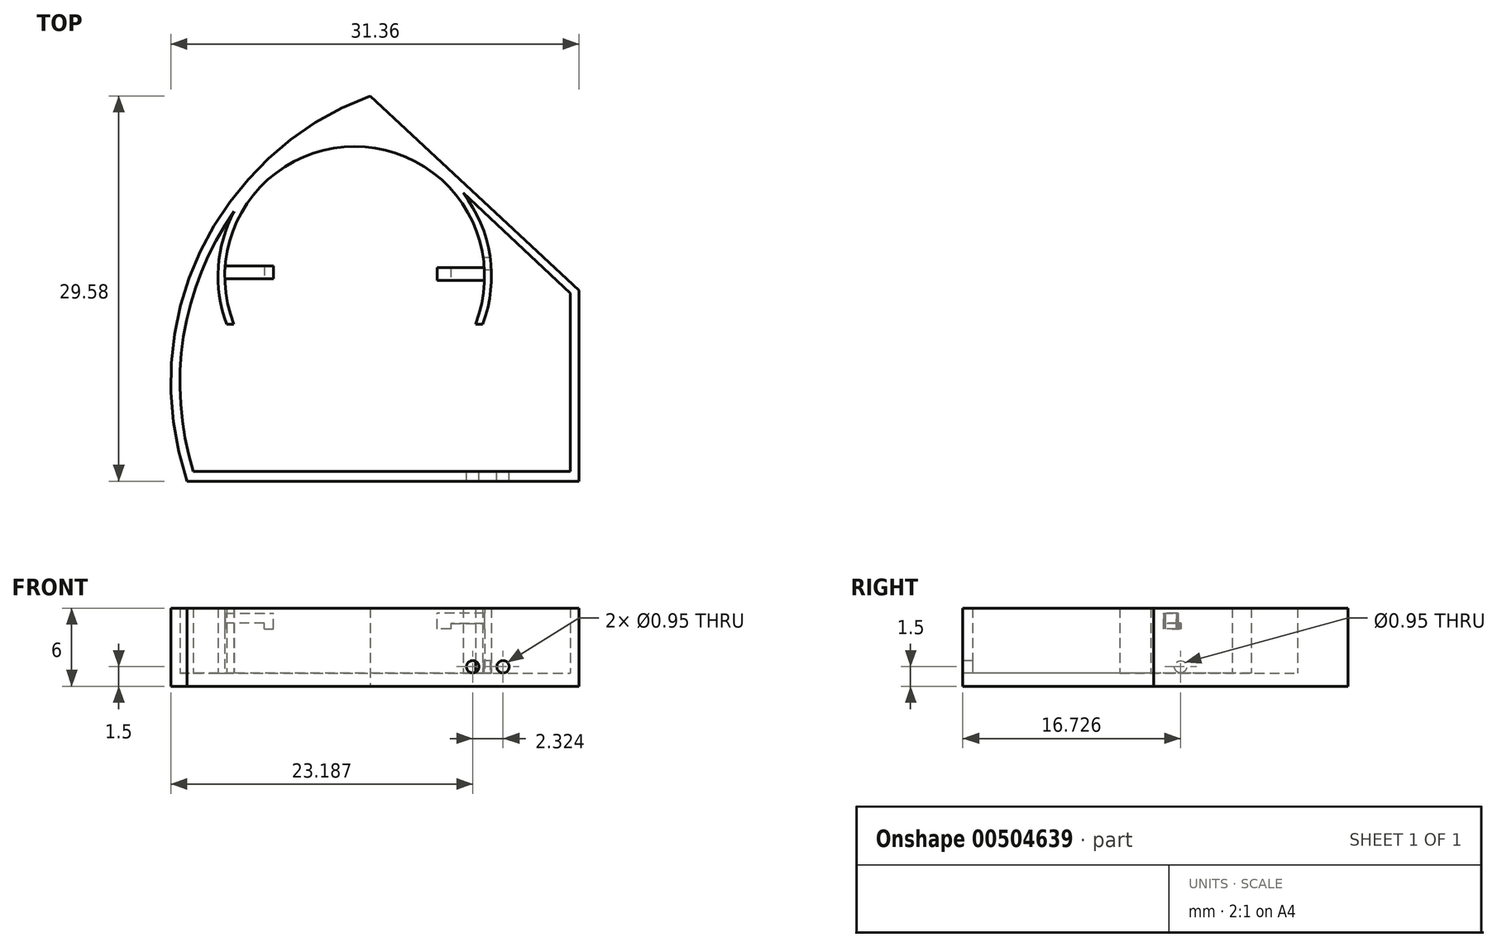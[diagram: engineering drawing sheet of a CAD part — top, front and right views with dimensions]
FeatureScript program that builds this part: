
annotation { "Feature Type Name" : "Feature", "Feature Type Description" : "" }
export const myFeature = defineFeature(function(context is Context, id is Id, definition is map)
    precondition{}
    {
        {
            var Q0;
            Q0=qCreatedBy(makeId("Top.planeOp"),FACE);
            var sketch = newSketch(context, id + "F0", { "sketchPlane" : qUnion([Q0])});
            skCircle(sketch, "E0", {"center": v(-9.38, 8.18) * mm, "radius": 9.97 * mm});
            skArc(sketch, "E1", {"start": v(-3.54, 16.9) * mm, "mid": v(-16.56, 0.52) * mm, "end": v(-1.05, 14.58) * mm});
            skArc(sketch, "E2", {"start": v(-18.63, 13.15) * mm, "mid": v(-22.58, 3.14) * mm, "end": v(-21.5, -7.56) * mm});
            skLineSegment(sketch, "E3", {"start": v(-21.76, -6.8) * mm, "end": v(7.86, -6.8) * mm});
            skLineSegment(sketch, "E4", {"start": v(-1.05, 14.58) * mm, "end": v(7.86, 6.22) * mm});
            skLineSegment(sketch, "E5", {"start": v(-1.05, 14.58) * mm, "end": v(-8.2, 21.27) * mm});
            skArc(sketch, "E6", {"start": v(-8.2, 22.02) * mm, "mid": v(-21.23, 10.08) * mm, "end": v(-22.25, -7.56) * mm});
            skLineSegment(sketch, "E7", {"start": v(-22.25, -7.56) * mm, "end": v(7.86, -7.56) * mm});
            skLineSegment(sketch, "E8", {"start": v(-8.2, 22.02) * mm, "end": v(7.86, 7.1) * mm});
            skLineSegment(sketch, "E9", {"start": v(7.18, 7.73) * mm, "end": v(7.18, -7.56) * mm});
            skLineSegment(sketch, "E10", {"start": v(7.86, 6.22) * mm, "end": v(7.86, -6.8) * mm});
            skLineSegment(sketch, "E11", {"start": v(7.86, 6.22) * mm, "end": v(7.86, 7.1) * mm});
            skLineSegment(sketch, "E12", {"start": v(7.86, -6.8) * mm, "end": v(7.86, -7.56) * mm});
            skLineSegment(sketch, "E13", {"start": v(-19.22, 4.5) * mm, "end": v(-18.65, 4.5) * mm});
            skLineSegment(sketch, "E14", {"start": v(-0.1, 4.5) * mm, "end": v(0.46, 4.5) * mm});
            skArc(sketch, "E15.trimOffspring", {"start": v(-7.63, 21.49) * mm, "mid": v(-7.91, 21.38) * mm, "end": v(-8.2, 21.27) * mm});
            skPoint(sketch, "E16.trimOffspring.end.orphan", {"position": v(22.56, -6.57) * mm});
            skSolve(sketch);
        }
        {
            var Q0;
            Q0=qCreatedBy(makeId("Top.planeOp"),FACE);
            cPlane(context, id + "F1", {"entities" : qUnion([Q0]), "cplaneType" : CPlaneType.OFFSET, "offset" : 5.6 * mm, "width" : 150 * mm, "height" : 150 * mm});
        }
        {
            var Q0;
            {var subQ0=sQuery(id+"F0.wireOp",EDGE,"E10");Q0=makeQuery(id+"F0.imprint","IMPRINT",FACE,{"disambiguationData":[TD([[makeQuery(id+"F0.imprint","IMPRINT",EDGE,{"derivedFrom":subQ0}),-1.0]])]});}
            var Q1;
            {var subQ0=sQuery(id+"F0.wireOp",EDGE,"E3");var subQ1=sQuery(id+"F0.wireOp",EDGE,"E2");var subQ2=makeQuery(id+"F0.imprint","INTERSECT",VERTEX,{"derivedFrom":[subQ1,subQ0]});Q1=makeQuery(id+"F0.imprint","IMPRINT",FACE,{"disambiguationData":[TD([[makeQuery(id+"F0.imprint","IMPRINT",EDGE,{"disambiguationData":[TD([[subQ2,-1.0]])],"derivedFrom":subQ1}),1.0]])]});}
            var Q2;
            {var subQ0=sQuery(id+"F0.wireOp",EDGE,"E11");Q2=makeQuery(id+"F0.imprint","IMPRINT",FACE,{"disambiguationData":[TD([[makeQuery(id+"F0.imprint","IMPRINT",EDGE,{"derivedFrom":subQ0}),1.0]])]});}
            var Q3;
            {var subQ0=sQuery(id+"F0.wireOp",EDGE,"E5");var subQ3=sQuery(id+"F0.wireOp",EDGE,"E2");var subQ4=makeQuery(id+"F0.imprint","INTERSECT",VERTEX,{"derivedFrom":[subQ3,subQ0]});Q3=makeQuery(id+"F0.imprint","IMPRINT",FACE,{"disambiguationData":[TD([[makeQuery(id+"F0.imprint","IMPRINT",EDGE,{"disambiguationData":[TD([[subQ4,1.0]])],"derivedFrom":subQ3}),1.0]])]});}
            var Q4;
            {var subQ0=sQuery(id+"F0.wireOp",EDGE,"E12");Q4=makeQuery(id+"F0.imprint","IMPRINT",FACE,{"disambiguationData":[TD([[makeQuery(id+"F0.imprint","IMPRINT",EDGE,{"derivedFrom":subQ0}),-1.0]])]});}
            var Q5;
            {var subQ0=sQuery(id+"F0.wireOp",EDGE,"E5");var subQ8=sQuery(id+"F0.wireOp",EDGE,"E1");var subQ10=makeQuery(id+"F0.imprint","INTERSECT",VERTEX,{"derivedFrom":[subQ8,subQ0]});Q5=makeQuery(id+"F0.imprint","IMPRINT",FACE,{"disambiguationData":[TD([[makeQuery(id+"F0.imprint","IMPRINT",EDGE,{"disambiguationData":[TD([[subQ10,-1.0]])],"derivedFrom":subQ8}),-1.0]])]});}
            var Q6;
            {var subQ4=sQuery(id+"F0.wireOp",EDGE,"zcf4CaVi-9V9S-3gAH-KYeD-Rh70sNSUDDbX");Q6=makeQuery(id+"F0.imprint","IMPRINT",FACE,{"disambiguationData":[TD([[makeQuery(id+"F0.imprint","IMPRINT",EDGE,{"derivedFrom":subQ4}),-1.0]])]});}
            var Q7;
            {var subQ5=sQuery(id+"F0.wireOp",EDGE,"E13");Q7=makeQuery(id+"F0.imprint","IMPRINT",FACE,{"disambiguationData":[TD([[makeQuery(id+"F0.imprint","IMPRINT",EDGE,{"derivedFrom":subQ5}),1.0]])]});}
            var Q8;
            {var subQ3=sQuery(id+"F0.wireOp",EDGE,"E15.trimOffspring");Q8=makeQuery(id+"F0.imprint","IMPRINT",FACE,{"disambiguationData":[TD([[makeQuery(id+"F0.imprint","IMPRINT",EDGE,{"derivedFrom":subQ3}),1.0]])]});}
            extrude(context, id + "F2", {"entities" : qUnion([Q0, Q1, Q2, Q3, Q4, Q5, Q6, Q7, Q8]), "depth" : 6 * mm, "offsetDistance" : 25 * mm});
        }
        {
            var Q0;
            Q0=makeQuery(id+"F2.opExtrude","SWEPT_FACE",FACE,{"disambiguationData":[OSD([sQuery(id+"F0.wireOp",EDGE,"E3")])]});
            var sketch = newSketch(context, id + "F3", { "sketchPlane" : qUnion([Q0])});
            skCircle(sketch, "E17", {"center": v(0.31, 1.5) * mm, "radius": 0.47 * mm});
            skCircle(sketch, "E18", {"center": v(-2.01, 1.5) * mm, "radius": 0.47 * mm});
            skSolve(sketch);
        }
        {
            var Q0;
            Q0=qCreatedBy(id+"F1.planeOp",FACE);
            var sketch = newSketch(context, id + "F4", { "sketchPlane" : qUnion([Q0])});
            skLineSegment(sketch, "E19.bottom", {"start": v(-19.62, 8.98) * mm, "end": v(-15.62, 8.98) * mm});
            skLineSegment(sketch, "E19.top", {"start": v(-19.62, 7.98) * mm, "end": v(-15.62, 7.98) * mm});
            skLineSegment(sketch, "E19.left", {"start": v(-19.62, 8.98) * mm, "end": v(-19.62, 7.98) * mm});
            skLineSegment(sketch, "E19.right", {"start": v(-15.62, 8.98) * mm, "end": v(-15.62, 7.98) * mm});
            skLineSegment(sketch, "E20.bottom", {"start": v(0.96, 8.85) * mm, "end": v(-3.04, 8.85) * mm});
            skLineSegment(sketch, "E20.top", {"start": v(0.96, 7.85) * mm, "end": v(-3.04, 7.85) * mm});
            skLineSegment(sketch, "E20.left", {"start": v(0.96, 8.85) * mm, "end": v(0.96, 7.85) * mm});
            skLineSegment(sketch, "E20.right", {"start": v(-3.04, 8.85) * mm, "end": v(-3.04, 7.85) * mm});
            skSolve(sketch);
        }
        {
            var Q0;
            Q0=makeQuery(id+"F4.imprint","IMPRINT",FACE,{"disambiguationData":[TD([[makeQuery(id+"F4.imprint","IMPRINT",EDGE,{"derivedFrom":sQuery(id+"F4.wireOp",EDGE,"E20.bottom")}),1.0]])]});
            var Q1;
            Q1=makeQuery(id+"F4.imprint","IMPRINT",FACE,{"disambiguationData":[TD([[makeQuery(id+"F4.imprint","IMPRINT",EDGE,{"derivedFrom":sQuery(id+"F4.wireOp",EDGE,"E19.bottom")}),-1.0]])]});
            extrude(context, id + "F5", {"entities" : qUnion([Q0, Q1]), "operationType" : NewBodyOperationType.ADD, "oppositeDirection" : true, "depth" : 1.2 * mm, "offsetDistance" : 25 * mm});
        }
        {
            var Q0;
            Q0=makeQuery(id+"F3.imprint","IMPRINT",FACE,{"disambiguationData":[TD([[makeQuery(id+"F3.imprint","IMPRINT",EDGE,{"derivedFrom":sQuery(id+"F3.wireOp",EDGE,"E17")}),1.0]])]});
            var Q1;
            Q1=makeQuery(id+"F3.imprint","IMPRINT",FACE,{"disambiguationData":[TD([[makeQuery(id+"F3.imprint","IMPRINT",EDGE,{"derivedFrom":sQuery(id+"F3.wireOp",EDGE,"E18")}),1.0]])]});
            extrude(context, id + "F6", {"entities" : qUnion([Q0, Q1]), "operationType" : NewBodyOperationType.REMOVE, "oppositeDirection" : true, "depth" : 1 * mm, "offsetDistance" : 25 * mm});
        }
        {
            var Q0;
            Q0=makeQuery(id+"F5.opExtrude","SWEPT_FACE",FACE,{"disambiguationData":[OSD([sQuery(id+"F4.wireOp",EDGE,"E19.top")])]});
            var sketch = newSketch(context, id + "F7", { "sketchPlane" : qUnion([Q0])});
            skLineSegment(sketch, "E21", {"start": v(-16.33, 4.4) * mm, "end": v(-16.33, 4.84) * mm});
            skLineSegment(sketch, "E22", {"start": v(-16.33, 4.84) * mm, "end": v(-19.35, 4.84) * mm});
            skLineSegment(sketch, "E23", {"start": v(-19.35, 4.84) * mm, "end": v(-19.35, 4.4) * mm});
            skLineSegment(sketch, "E24", {"start": v(-19.35, 4.4) * mm, "end": v(-16.33, 4.4) * mm});
            skSolve(sketch);
        }
        {
            var Q0;
            Q0=makeQuery(id+"F7.imprint","IMPRINT",FACE,{"disambiguationData":[TD([[makeQuery(id+"F7.imprint","IMPRINT",EDGE,{"derivedFrom":sQuery(id+"F7.wireOp",EDGE,"E21")}),1.0]])]});
            extrude(context, id + "F8", {"entities" : qUnion([Q0]), "operationType" : NewBodyOperationType.REMOVE, "oppositeDirection" : true, "depth" : 1.2 * mm, "offsetDistance" : 25 * mm});
        }
        {
            var Q0;
            Q0=makeQuery(id+"F5.opExtrude","SWEPT_FACE",FACE,{"disambiguationData":[OSD([sQuery(id+"F4.wireOp",EDGE,"E20.top")])]});
            var sketch = newSketch(context, id + "F9", { "sketchPlane" : qUnion([Q0])});
            skLineSegment(sketch, "E25", {"start": v(-2, 4.4) * mm, "end": v(-2, 4.83) * mm});
            skLineSegment(sketch, "E26", {"start": v(-2, 4.83) * mm, "end": v(0.6, 4.83) * mm});
            skLineSegment(sketch, "E27", {"start": v(0.6, 4.83) * mm, "end": v(0.6, 4.4) * mm});
            skLineSegment(sketch, "E28", {"start": v(0.6, 4.4) * mm, "end": v(-2, 4.4) * mm});
            skSolve(sketch);
        }
        {
            var Q0;
            Q0=makeQuery(id+"F9.imprint","IMPRINT",FACE,{"disambiguationData":[TD([[makeQuery(id+"F9.imprint","IMPRINT",EDGE,{"derivedFrom":sQuery(id+"F9.wireOp",EDGE,"E25")}),-1.0]])]});
            extrude(context, id + "F10", {"entities" : qUnion([Q0]), "operationType" : NewBodyOperationType.REMOVE, "oppositeDirection" : true, "depth" : 1.2 * mm, "offsetDistance" : 25 * mm});
        }
        {
            var Q0;
            {var subQ0=sQuery(id+"F0.wireOp",EDGE,"E2");var subQ1=sQuery(id+"F0.wireOp",EDGE,"E1");var subQ2=makeQuery(id+"F0.imprint","INTERSECT",VERTEX,{"derivedFrom":[subQ1,subQ0]});Q0=makeQuery(id+"F0.imprint","IMPRINT",FACE,{"disambiguationData":[TD([[makeQuery(id+"F0.imprint","IMPRINT",EDGE,{"disambiguationData":[TD([[subQ2,-1.0]])],"derivedFrom":subQ1}),-1.0]])]});}
            var Q1;
            {var subQ0=sQuery(id+"F0.wireOp",EDGE,"E0");var subQ1=makeQuery(id+"F0.imprint","INTERSECT",VERTEX,{"derivedFrom":[subQ0,sQuery(id+"F0.wireOp",EDGE,"E13")]});Q1=makeQuery(id+"F0.imprint","IMPRINT",FACE,{"disambiguationData":[TD([[makeQuery(id+"F0.imprint","IMPRINT",EDGE,{"disambiguationData":[TD([[subQ1,-1.0]])],"derivedFrom":subQ0}),1.0]])]});}
            var Q2;
            {var subQ0=sQuery(id+"F0.wireOp",EDGE,"E13");Q2=makeQuery(id+"F0.imprint","IMPRINT",FACE,{"disambiguationData":[TD([[makeQuery(id+"F0.imprint","IMPRINT",EDGE,{"derivedFrom":subQ0}),-1.0]])]});}
            extrude(context, id + "F11", {"entities" : qUnion([Q0, Q1, Q2]), "operationType" : NewBodyOperationType.ADD, "depth" : 1 * mm, "offsetDistance" : 25 * mm});
        }
        {
            var Q0;
            Q0=qCreatedBy(makeId("Right.planeOp"),FACE);
            cPlane(context, id + "F12", {"entities" : qUnion([Q0]), "cplaneType" : CPlaneType.OFFSET, "offset" : 1.2 * mm, "width" : 150 * mm, "height" : 150 * mm});
        }
        {
            var Q0;
            Q0=qCreatedBy(id+"F12.planeOp",FACE);
            var sketch = newSketch(context, id + "F13", { "sketchPlane" : qUnion([Q0])});
            skCircle(sketch, "E29", {"center": v(9.17, 1.5) * mm, "radius": 0.47 * mm});
            skSolve(sketch);
        }
        {
            var Q0;
            Q0=makeQuery(id+"F13.imprint","IMPRINT",FACE,{"disambiguationData":[TD([[makeQuery(id+"F13.imprint","IMPRINT",EDGE,{"derivedFrom":sQuery(id+"F13.wireOp",EDGE,"E29")}),1.0]])]});
            extrude(context, id + "F14", {"entities" : qUnion([Q0]), "operationType" : NewBodyOperationType.REMOVE, "oppositeDirection" : true, "depth" : 2 * mm, "offsetDistance" : 25 * mm});
        }
    });
